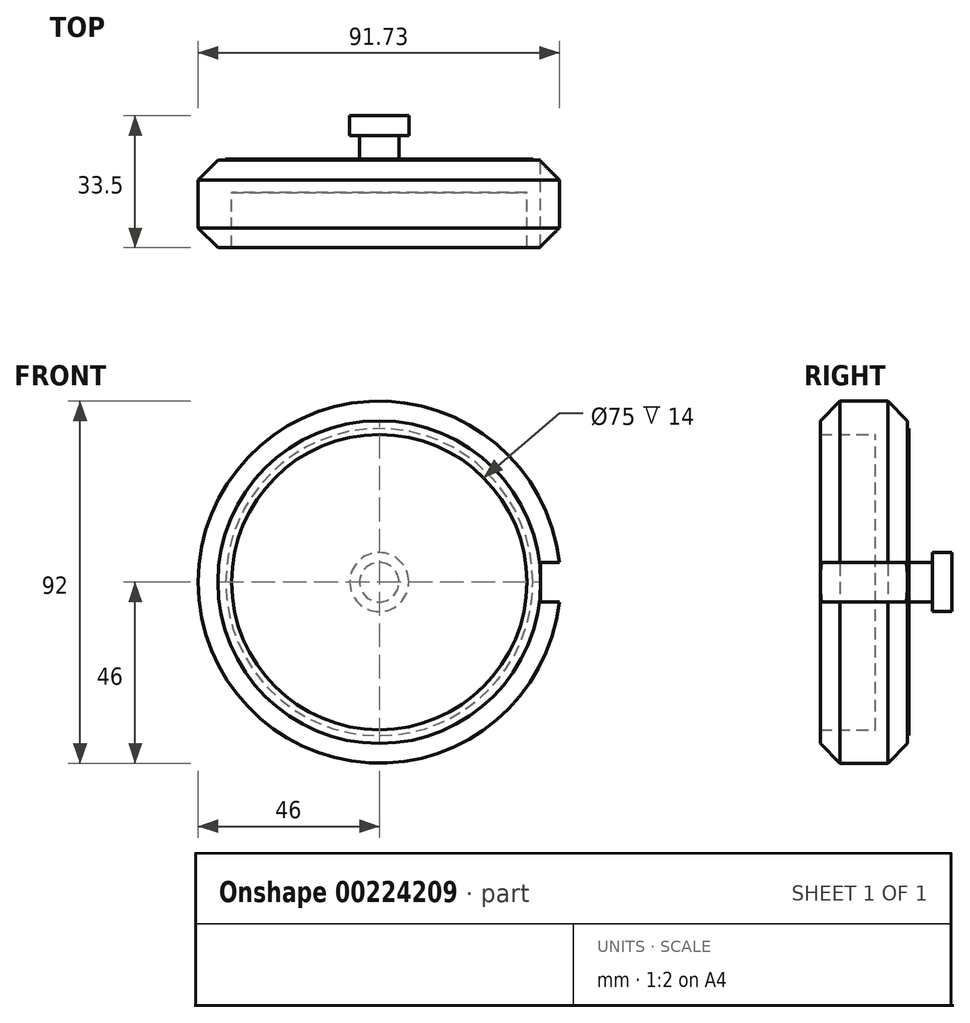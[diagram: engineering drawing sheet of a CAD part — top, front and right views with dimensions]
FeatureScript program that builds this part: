
annotation { "Feature Type Name" : "Feature", "Feature Type Description" : "" }
export const myFeature = defineFeature(function(context is Context, id is Id, definition is map)
    precondition{}
    {
        {
            var Q0;
            Q0=qCreatedBy(makeId("Front.planeOp"),FACE);
            var sketch = newSketch(context, id + "F0", { "sketchPlane" : qUnion([Q0])});
            skCircle(sketch, "E0", {"center": v(0, 0) * mm, "radius": 46 * mm});
            skSolve(sketch);
        }
        {
            var Q0;
            Q0 = qSketchRegion(id + "F0", true);
            extrude(context, id + "F1", {"entities" : qUnion([Q0]), "depth" : 22.5 * mm});
        }
        {
            var Q0;
            Q0=makeQuery(id+"F1.opExtrude","CAP_FACE",FACE,{"disambiguationData":[OSD([sQuery(id+"F0.wireOp",EDGE,"E0")])],"isStart":false});
            shell(context, id + "F2", {"entities" : qUnion([Q0]), "thickness" : 8.5 * mm});
        }
        {
            var Q0;
            Q0=qCreatedBy(makeId("Front.planeOp"),FACE);
            var sketch = newSketch(context, id + "F3", { "sketchPlane" : qUnion([Q0])});
            skCircle(sketch, "E1", {"center": v(0, 0) * mm, "radius": 55.5 * mm});
            skCircle(sketch, "E2", {"center": v(0, 0) * mm, "radius": 39 * mm});
            skSolve(sketch);
        }
        {
            var Q0;
            Q0=makeQuery(id+"F3.imprint","IMPRINT",FACE,{"disambiguationData":[TD([[makeQuery(id+"F3.imprint","IMPRINT",EDGE,{"derivedFrom":sQuery(id+"F3.wireOp",EDGE,"E1")}),1.0]])]});
            extrude(context, id + "F4", {"entities" : qUnion([Q0]), "operationType" : NewBodyOperationType.REMOVE, "depth" : .3 * mm});
        }
        {
            var Q0;
            Q0=qCreatedBy(makeId("Front.planeOp"),FACE);
            var sketch = newSketch(context, id + "F5", { "sketchPlane" : qUnion([Q0])});
            skCircle(sketch, "E3", {"center": v(0, 0) * mm, "radius": 5 * mm});
            skSolve(sketch);
        }
        {
            var Q0;
            Q0 = qSketchRegion(id + "F5", true);
            extrude(context, id + "F6", {"entities" : qUnion([Q0]), "operationType" : NewBodyOperationType.ADD, "oppositeDirection" : true, "depth" : 6 * mm});
        }
        {
            var Q0;
            Q0=makeQuery(id+"F6.opExtrude","CAP_FACE",FACE,{"disambiguationData":[OSD([sQuery(id+"F5.wireOp",EDGE,"E3")])],"isStart":false});
            var sketch = newSketch(context, id + "F7", { "sketchPlane" : qUnion([Q0])});
            skCircle(sketch, "E4", {"center": v(0, 0) * mm, "radius": 7.5 * mm});
            skSolve(sketch);
        }
        {
            var Q0;
            Q0=makeQuery(id+"F7.imprint","IMPRINT",FACE,{"disambiguationData":[TD([[makeQuery(id+"F7.imprint","IMPRINT",EDGE,{"derivedFrom":sQuery(id+"F7.wireOp",EDGE,"E4")}),1.0]])]});
            var Q1;
            Q1=makeQuery(id+"F7.imprint","IMPRINT",FACE,{"disambiguationData":[TD([[makeQuery(id+"F7.imprint","IMPRINT",EDGE,{"derivedFrom":makeQuery(id+"F6.opExtrude","CAP_EDGE",EDGE,{"disambiguationData":[OSD([sQuery(id+"F5.wireOp",EDGE,"E3")])],"isStart":false})}),-1.0]])]});
            extrude(context, id + "F8", {"entities" : qUnion([Q0, Q1]), "operationType" : NewBodyOperationType.ADD, "depth" : 5 * mm});
        }
        {
            var Q0;
            Q0=makeQuery(id+"F4.boolean.opBoolean","INTERSECT",EDGE,{"derivedFrom":[makeQuery(id+"F1.opExtrude","SWEPT_FACE",FACE,{"disambiguationData":[OSD([sQuery(id+"F0.wireOp",EDGE,"E0")])]}),makeQuery(id+"F4.opExtrude","CAP_FACE",FACE,{"disambiguationData":[OSD([sQuery(id+"F3.wireOp",EDGE,"E1"),sQuery(id+"F3.wireOp",EDGE,"E2")])],"isStart":false})]});
            var Q1;
            Q1=makeQuery(id+"F1.opExtrude","CAP_EDGE",EDGE,{"disambiguationData":[OSD([sQuery(id+"F0.wireOp",EDGE,"E0")])],"isStart":false});
            chamfer(context, id + "F9", {"entities" : qUnion([Q0, Q1]), "chamferType" : ChamferType.OFFSET_ANGLE, "width" : 5 * mm, "oppositeDirection" : false, "angle" : 45 * degree, "tangentPropagation" : true});
        }
        {
            var Q0;
            Q0=qCreatedBy(makeId("Front.planeOp"),FACE);
            var sketch = newSketch(context, id + "F10", { "sketchPlane" : qUnion([Q0])});
            skLineSegment(sketch, "E5.bottom", {"start": v(41, 5) * mm, "end": v(52.57, 5) * mm});
            skLineSegment(sketch, "E5.top", {"start": v(41, -5) * mm, "end": v(52.57, -5) * mm});
            skLineSegment(sketch, "E5.left", {"start": v(41, 5) * mm, "end": v(41, -5) * mm});
            skLineSegment(sketch, "E5.right", {"start": v(52.57, 5) * mm, "end": v(52.57, -5) * mm});
            skSolve(sketch);
        }
        {
            var Q0;
            Q0 = qSketchRegion(id + "F10", true);
            extrude(context, id + "F11", {"entities" : qUnion([Q0]), "operationType" : NewBodyOperationType.REMOVE, "endBound" : BoundingType.THROUGH_ALL, "depth" : 25 * mm});
        }
        {
            var Q0;
            Q0=qCreatedBy(makeId("Right.planeOp"),FACE);
            var sketch = newSketch(context, id + "F12", { "sketchPlane" : qUnion([Q0])});
            skLineSegment(sketch, "E6", {"start": v(42.48, 0) * mm, "end": v(-53.6, 0) * mm, "construction": true});
            skSolve(sketch);
        }
    });
